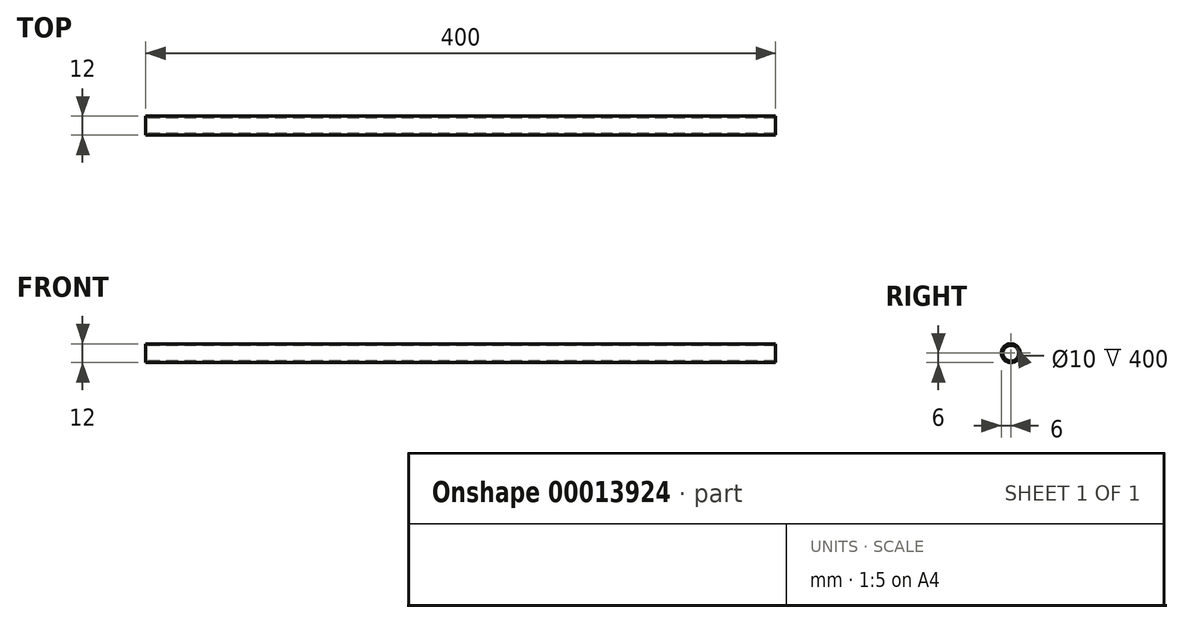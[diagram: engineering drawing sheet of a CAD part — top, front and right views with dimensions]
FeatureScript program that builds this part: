
annotation { "Feature Type Name" : "Feature", "Feature Type Description" : "" }
export const myFeature = defineFeature(function(context is Context, id is Id, definition is map)
    precondition{}
    {
        {
            var Q0;
            Q0=qCreatedBy(makeId("Right.planeOp"),FACE);
            var sketch = newSketch(context, id + "F0", { "sketchPlane" : qUnion([Q0])});
            skCircle(sketch, "E0", {"center": v(0, 0) * mm, "radius": 6 * mm});
            skCircle(sketch, "E1", {"center": v(0, 0) * mm, "radius": 5 * mm});
            skSolve(sketch);
        }
        {
            var Q0;
            Q0 = qSketchRegion(id + "F0", true);
            extrude(context, id + "F1", {"entities" : qUnion([Q0]), "depth" : 400 * mm});
        }
    });
